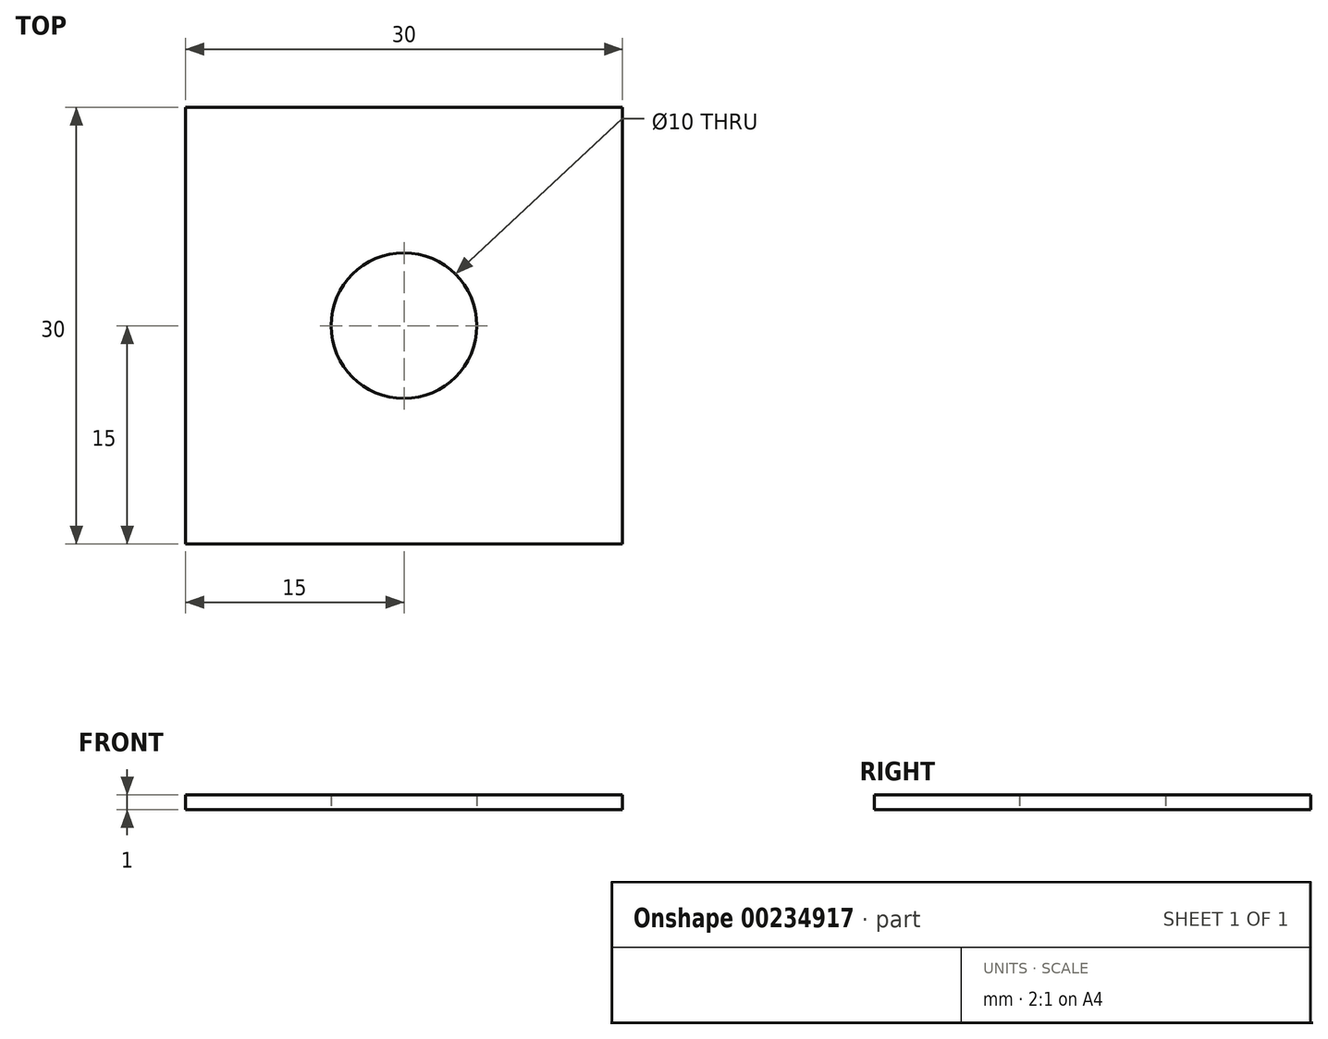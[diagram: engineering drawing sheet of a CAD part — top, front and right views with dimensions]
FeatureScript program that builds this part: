
annotation { "Feature Type Name" : "Feature", "Feature Type Description" : "" }
export const myFeature = defineFeature(function(context is Context, id is Id, definition is map)
    precondition{}
    {
        {
            var Q0;
            Q0=qCreatedBy(makeId("Top.planeOp"),FACE);
            var sketch = newSketch(context, id + "F0", { "sketchPlane" : qUnion([Q0])});
            skLineSegment(sketch, "E0.bottom", {"start": v(15, 15) * mm, "end": v(-15, 15) * mm});
            skLineSegment(sketch, "E0.top", {"start": v(15, -15) * mm, "end": v(-15, -15) * mm});
            skLineSegment(sketch, "E0.left", {"start": v(15, 15) * mm, "end": v(15, -15) * mm});
            skLineSegment(sketch, "E0.right", {"start": v(-15, 15) * mm, "end": v(-15, -15) * mm});
            skPoint(sketch, "E0.middle", {"position": v(0, 0) * mm});
            skCircle(sketch, "E1", {"center": v(0, 0) * mm, "radius": 5 * mm});
            skSolve(sketch);
        }
        {
            var Q0;
            Q0 = qSketchRegion(id + "F0", true);
            extrude(context, id + "F1", {"entities" : qUnion([Q0]), "depth" : 1 * mm});
        }
    });
